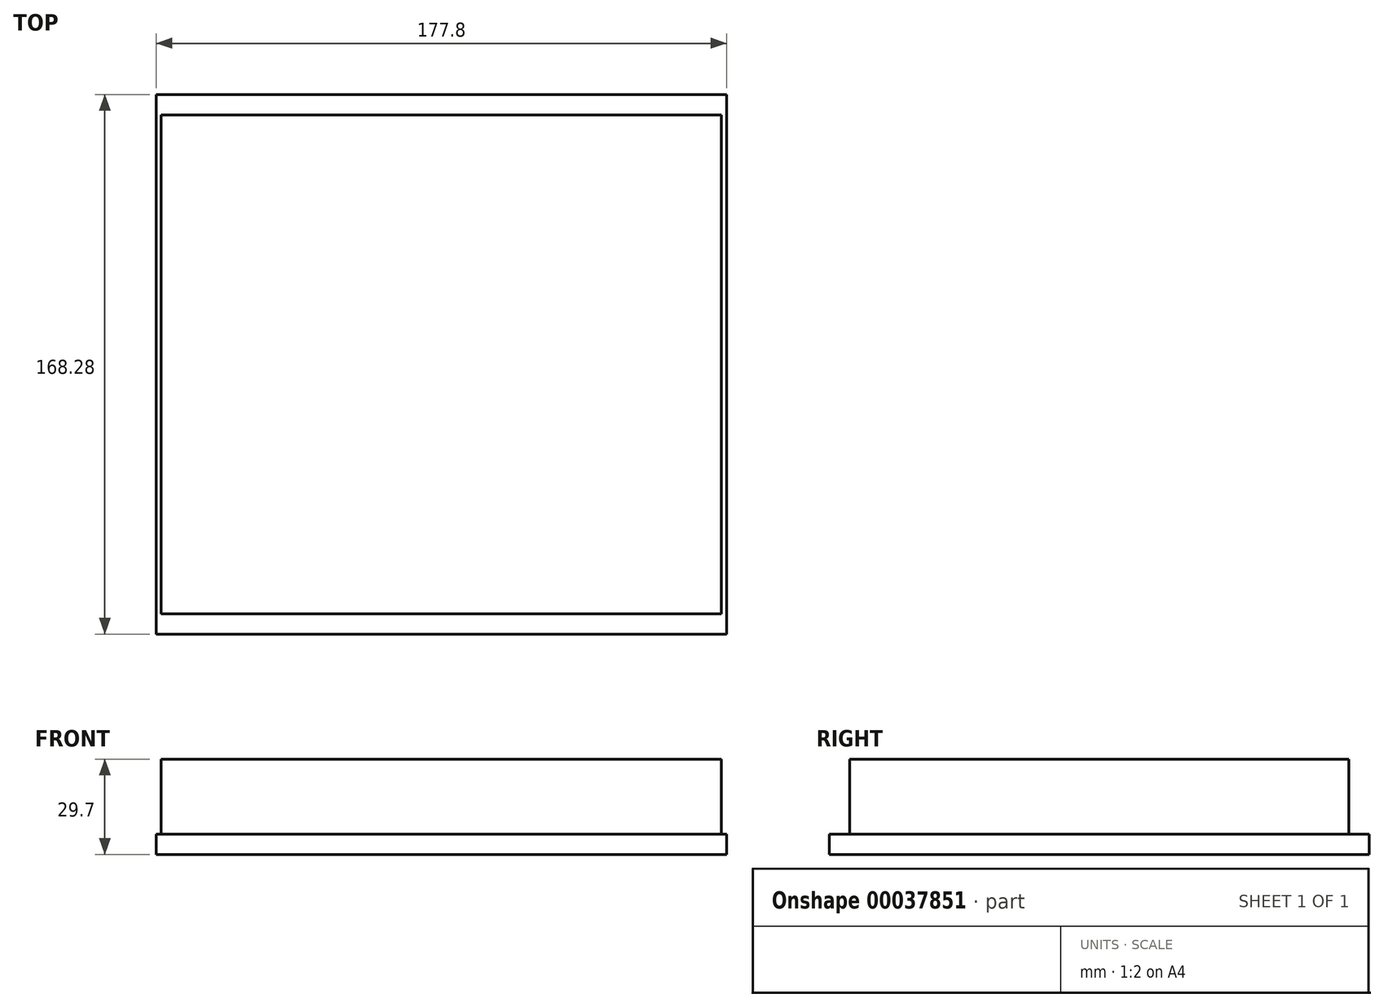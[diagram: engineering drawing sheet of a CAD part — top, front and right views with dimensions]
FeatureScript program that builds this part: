
annotation { "Feature Type Name" : "Feature", "Feature Type Description" : "" }
export const myFeature = defineFeature(function(context is Context, id is Id, definition is map)
    precondition{}
    {
        {
            var Q0;
            Q0=qCreatedBy(makeId("Top.planeOp"),FACE);
            var sketch = newSketch(context, id + "F0", { "sketchPlane" : qUnion([Q0])});
            skLineSegment(sketch, "E0.bottom", {"start": v(0, 0) * mm, "end": v(177.8, 0) * mm});
            skLineSegment(sketch, "E0.top", {"start": v(0, 168.28) * mm, "end": v(177.8, 168.28) * mm});
            skLineSegment(sketch, "E0.left", {"start": v(0, 0) * mm, "end": v(0, 168.28) * mm});
            skLineSegment(sketch, "E0.right", {"start": v(177.8, 0) * mm, "end": v(177.8, 168.28) * mm});
            skSolve(sketch);
        }
        {
            var Q0;
            Q0 = qSketchRegion(id + "F0", true);
            extrude(context, id + "F1", {"entities" : qUnion([Q0]), "depth" : 6.35 * mm});
        }
        {
            var Q0;
            Q0=makeQuery(id+"F1.opExtrude","CAP_FACE",FACE,{"disambiguationData":[OSD([sQuery(id+"F0.wireOp",EDGE,"E0.bottom"),sQuery(id+"F0.wireOp",EDGE,"E0.top"),sQuery(id+"F0.wireOp",EDGE,"E0.left"),sQuery(id+"F0.wireOp",EDGE,"E0.right")])],"isStart":false});
            var sketch = newSketch(context, id + "F2", { "sketchPlane" : qUnion([Q0])});
            skLineSegment(sketch, "E1.rect.bottom", {"start": v(1.59, 161.93) * mm, "end": v(176.21, 161.93) * mm});
            skLineSegment(sketch, "E1.rect.top", {"start": v(1.59, 6.35) * mm, "end": v(176.21, 6.35) * mm});
            skLineSegment(sketch, "E1.rect.left", {"start": v(1.59, 161.93) * mm, "end": v(1.59, 6.35) * mm});
            skLineSegment(sketch, "E1.rect.right", {"start": v(176.21, 161.93) * mm, "end": v(176.21, 6.35) * mm});
            skPoint(sketch, "E1.rect.middle", {"position": v(88.9, 84.14) * mm});
            skLineSegment(sketch, "E2", {"start": v(88.9, 168.28) * mm, "end": v(88.9, 0) * mm, "construction": true});
            skSolve(sketch);
        }
        {
            var Q0;
            Q0 = qSketchRegion(id + "F2", true);
            extrude(context, id + "F3", {"entities" : qUnion([Q0]), "operationType" : NewBodyOperationType.ADD, "depth" : 23.35 * mm});
        }
    });
